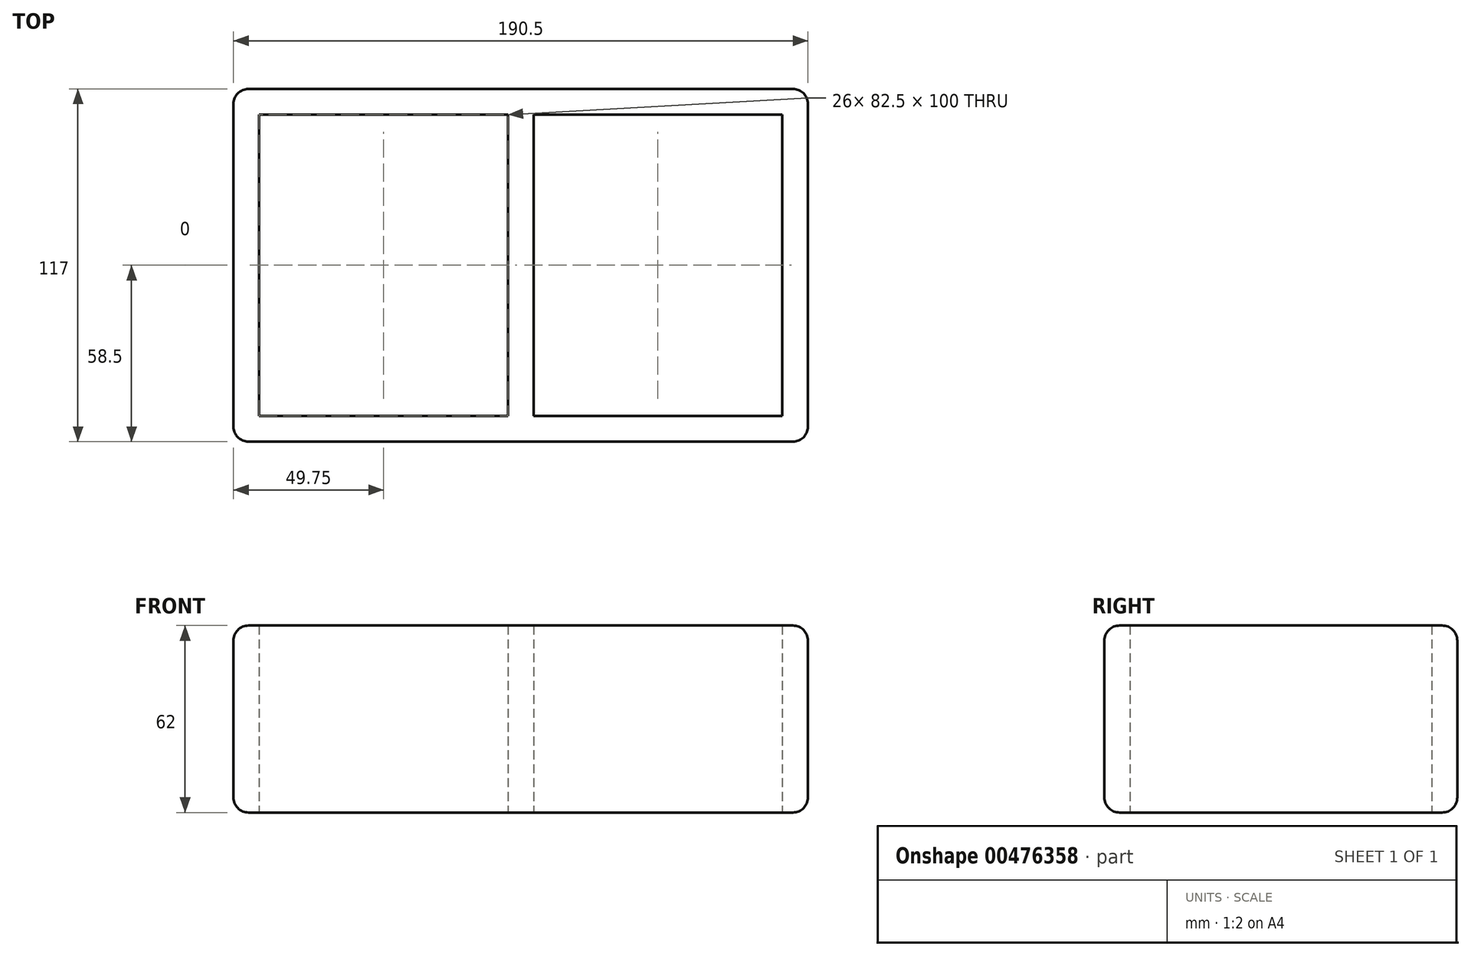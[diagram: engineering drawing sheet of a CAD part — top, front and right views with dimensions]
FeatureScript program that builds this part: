
annotation { "Feature Type Name" : "Feature", "Feature Type Description" : "" }
export const myFeature = defineFeature(function(context is Context, id is Id, definition is map)
    precondition{}
    {
        {
            var Q0;
            Q0=qCreatedBy(makeId("Top.planeOp"),FACE);
            var sketch = newSketch(context, id + "F0", { "sketchPlane" : qUnion([Q0])});
            skLineSegment(sketch, "E0.bottom", {"start": v(0, 0) * mm, "end": v(-190.5, 0) * mm});
            skLineSegment(sketch, "E0.top", {"start": v(0, 117) * mm, "end": v(-190.5, 117) * mm});
            skLineSegment(sketch, "E0.left", {"start": v(0, 0) * mm, "end": v(0, 117) * mm});
            skLineSegment(sketch, "E0.right", {"start": v(-190.5, 0) * mm, "end": v(-190.5, 117) * mm});
            skLineSegment(sketch, "E1.bottom", {"start": v(-8.5, 8.5) * mm, "end": v(-91, 8.5) * mm});
            skLineSegment(sketch, "E1.top", {"start": v(-8.5, 108.5) * mm, "end": v(-91, 108.5) * mm});
            skLineSegment(sketch, "E1.left", {"start": v(-8.5, 8.5) * mm, "end": v(-8.5, 108.5) * mm});
            skLineSegment(sketch, "E1.right", {"start": v(-182, 8.5) * mm, "end": v(-182, 108.5) * mm});
            skLineSegment(sketch, "E2", {"start": v(-99.5, 108.5) * mm, "end": v(-99.5, 8.5) * mm});
            skLineSegment(sketch, "E3", {"start": v(-91, 108.5) * mm, "end": v(-91, 8.5) * mm});
            skLineSegment(sketch, "E4.trimOffspring", {"start": v(-99.5, 108.5) * mm, "end": v(-182, 108.5) * mm});
            skLineSegment(sketch, "E5.trimOffspring", {"start": v(-99.5, 8.5) * mm, "end": v(-182, 8.5) * mm});
            skSolve(sketch);
        }
        {
            var Q0;
            Q0 = qSketchRegion(id + "F0", true);
            extrude(context, id + "F1", {"entities" : qUnion([Q0]), "depth" : 62 * mm});
        }
        {
            var Q0;
            Q0=makeQuery(id+"F1.opExtrude","CAP_EDGE",EDGE,{"disambiguationData":[OSD([sQuery(id+"F0.wireOp",EDGE,"E0.top")])],"isStart":false});
            var Q1;
            Q1=makeQuery(id+"F1.opExtrude","CAP_EDGE",EDGE,{"disambiguationData":[OSD([sQuery(id+"F0.wireOp",EDGE,"E0.top")])],"isStart":true});
            var Q2;
            Q2=makeQuery(id+"F1.opExtrude","CAP_EDGE",EDGE,{"disambiguationData":[OSD([sQuery(id+"F0.wireOp",EDGE,"E0.bottom")])],"isStart":false});
            var Q3;
            Q3=makeQuery(id+"F1.opExtrude","CAP_EDGE",EDGE,{"disambiguationData":[OSD([sQuery(id+"F0.wireOp",EDGE,"E0.bottom")])],"isStart":true});
            var Q4;
            Q4=makeQuery(id+"F1.opExtrude","CAP_EDGE",EDGE,{"disambiguationData":[OSD([sQuery(id+"F0.wireOp",EDGE,"E0.right")])],"isStart":true});
            var Q5;
            Q5=makeQuery(id+"F1.opExtrude","CAP_EDGE",EDGE,{"disambiguationData":[OSD([sQuery(id+"F0.wireOp",EDGE,"E0.right")])],"isStart":false});
            var Q6;
            Q6=makeQuery(id+"F1.opExtrude","CAP_EDGE",EDGE,{"disambiguationData":[OSD([sQuery(id+"F0.wireOp",EDGE,"E0.left")])],"isStart":true});
            var Q7;
            Q7=makeQuery(id+"F1.opExtrude","SWEPT_EDGE",EDGE,{"disambiguationData":[OSD([sQuery(id+"F0.wireOp",EDGE,"E0.bottom"),sQuery(id+"F0.wireOp",EDGE,"E0.left")])]});
            var Q8;
            Q8=makeQuery(id+"F1.opExtrude","CAP_EDGE",EDGE,{"disambiguationData":[OSD([sQuery(id+"F0.wireOp",EDGE,"E0.left")])],"isStart":false});
            var Q9;
            Q9=makeQuery(id+"F1.opExtrude","SWEPT_EDGE",EDGE,{"disambiguationData":[OSD([sQuery(id+"F0.wireOp",EDGE,"E0.top"),sQuery(id+"F0.wireOp",EDGE,"E0.left")])]});
            var Q10;
            Q10=makeQuery(id+"F1.opExtrude","SWEPT_EDGE",EDGE,{"disambiguationData":[OSD([sQuery(id+"F0.wireOp",EDGE,"E0.top"),sQuery(id+"F0.wireOp",EDGE,"E0.right")])]});
            var Q11;
            Q11=makeQuery(id+"F1.opExtrude","SWEPT_EDGE",EDGE,{"disambiguationData":[OSD([sQuery(id+"F0.wireOp",EDGE,"E0.bottom"),sQuery(id+"F0.wireOp",EDGE,"E0.right")])]});
            fillet(context, id + "F2", {"entities" : qUnion([Q0, Q1, Q2, Q3, Q4, Q5, Q6, Q7, Q8, Q9, Q10, Q11]), "radius" : 5 * mm, "tangentPropagation" : true, "allowEdgeOverflow" : false});
        }
    });
